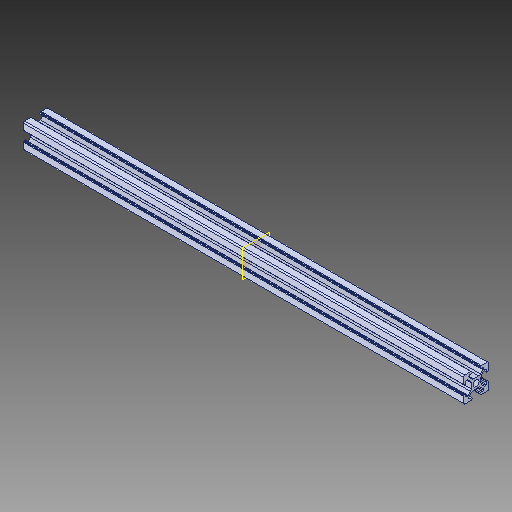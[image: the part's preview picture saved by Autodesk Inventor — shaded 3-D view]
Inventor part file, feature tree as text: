
AUTODESK INVENTOR PART (.ipt)
format: ipt  version: 2018 (Build 220112000, 112)  size: 355,840 bytes
history: native  units: in
note: dims shown in document units (in); Inventor stores cm internally (conversion verified against a paired STEP export)
features: extrude x1, plane x1, sketch x1, projected_geometry x1, fillet x1
ambient origin geometry x8: Origin, YZ Plane, XZ Plane, XY Plane, X Axis, Y Axis, Z Axis, Center Point
bodies: Solid1 (feature_tree)
feature tree (5):
  extrude  "Extrusion2"  [1 undecoded]
  plane  "Work Plane1"
  sketch  "Sketch3"  dims[d2=9.8425in d3=0.0in]
  projected_geometry  "Projected Loop2"
  fillet  "Fillet5"  [1 undecoded]
note: 2 required parameter values undecoded (feature->parameter linkage not recoverable at this tier; creation-order binding heuristic only, values carry confidence <= 0.55)
